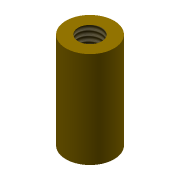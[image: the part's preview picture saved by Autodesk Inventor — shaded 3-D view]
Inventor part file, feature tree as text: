
AUTODESK INVENTOR PART (.ipt)
format: ipt  version: 2022 (Build 260153000, 153)  size: 78,848 bytes
history: native  units: mm
features: sketch x2, extrude x1, hole x1
ambient origin geometry x8: Origin, YZ Plane, XZ Plane, XY Plane, X Axis, Y Axis, Z Axis, Center Point
bodies: Solid1 (feature_tree)
feature tree (4):
  extrude  "Extrusion1"  Depth=10.0mm TaperAngle=0.0deg
  hole  "Hole1"  [1 undecoded]
  sketch  "Sketch1"  dims[d0=5.0mm d1=10.0mm d2=0.0mm]
  sketch  "Sketch2"  dims[d3=2.459mm d4=10.0mm d5=4.0mm d6=2.0mm d7=90.0deg d8=8.0mm d9=20.594885mm]
note: 1 required parameter value undecoded (feature->parameter linkage not recoverable at this tier; creation-order binding heuristic only, values carry confidence <= 0.55)
